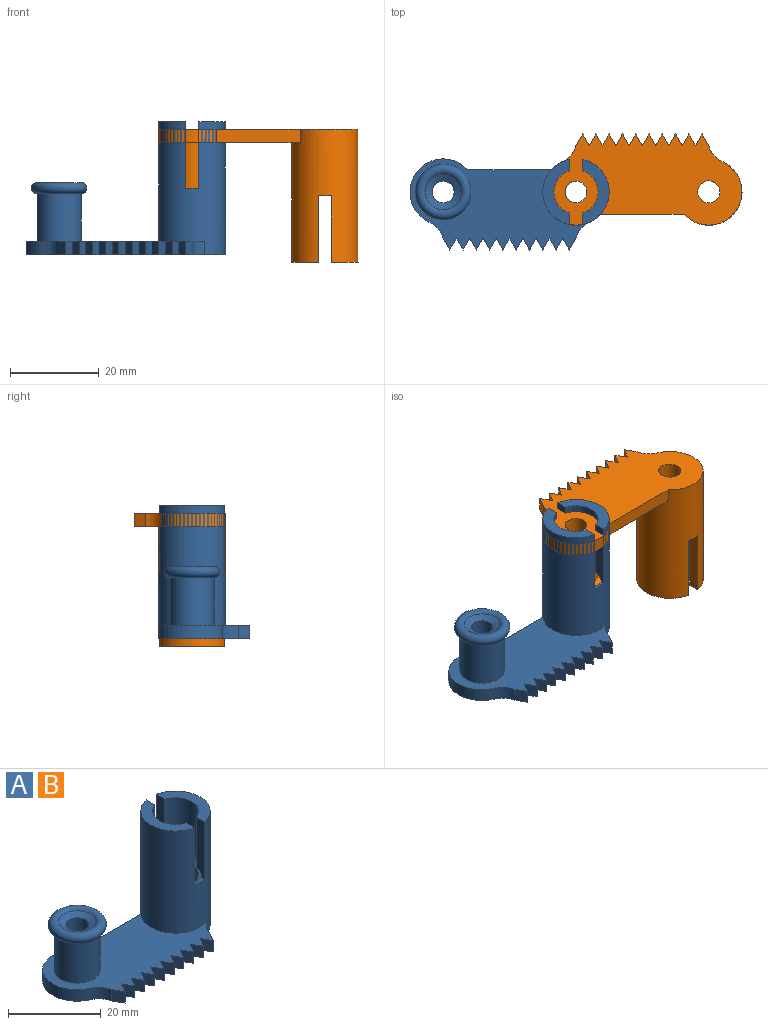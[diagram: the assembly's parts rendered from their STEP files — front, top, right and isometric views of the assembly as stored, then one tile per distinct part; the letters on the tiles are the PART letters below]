
ASSEMBLY  parts=2 mates=1
PART A: 45 faces, bbox 45x20.6x30 mm
  f0: sphere r=5mm, area 136mm2, adj f18,f22
  f1: cylinder r=5mm len=13.25mm, axis (0,0,-1), area 167.8mm2, adj f3,f6,f14,f17
  f2: cylinder r=5mm len=13.25mm, axis (0,0,-1), area 167.8mm2, adj f4,f5,f7,f17
  f3: plane 15x2.58mm, normal (-1,0,0), area 36.2mm2, adj f1,f11,f14,f15,f17
  f4: plane 15x2.58mm, normal (1,0,0), area 36.2mm2, adj f2,f7,f11,f15,f17
  f5: plane 15x2.58mm, normal (1,0,0), area 36.2mm2, adj f2,f7,f11,f16,f17
  f6: plane 15x2.58mm, normal (-1,0,0), area 36.2mm2, adj f1,f11,f14,f16,f17
  f7: plane 14.7x6mm, normal (0,0,1), area 41.5mm2, adj f2,f4,f5,f11
  f8: plane 40.44x20.58mm, normal (0,0,1), area 449.2mm2, adj f9,f10,f11,f13,f23,f24,f25,f26
  f9: plane 18.82x3mm, normal (0,1,0), area 56.5mm2, adj f8,f10,f11,f12
  f10: cylinder r=7.5mm len=14.4mm, axis (0,0,-1), area 80.5mm2, adj f8,f9,f12,f44
  f11: cylinder r=7.5mm len=30mm, axis (0,0,-1), area 1262.3mm2, adj f3,f4,f5,f6,f7,f8,f9,f12
  f12: plane 45x20.58mm, normal (0,0,-1), area 665.9mm2, adj f9,f10,f11,f21,f22,f23,f24,f25
  f13: cylinder r=5mm len=10.75mm, axis (0,0,-1), area 337.7mm2, adj f8,f19
  f14: plane 14.7x6mm, normal (0,0,1), area 41.5mm2, adj f1,f3,f6,f11
  f15: plane 3x0.92mm, normal (0,0,1), area 2.3mm2, adj f3,f4,f11,f17
  f16: plane 3x0.92mm, normal (0,0,1), area 2.3mm2, adj f5,f6,f11,f17
  f17: torus R=5mm, axis (0,0,1), area 194.5mm2, adj f1,f2,f3,f4,f5,f6,f15,f16
  f18: cylinder r=5mm len=10mm, axis (0,0,-1), area 164.9mm2, adj f0,f17
  f19: torus R=5.01mm, axis (0,0,1), area 175.8mm2, adj f13,f20
  f20: cone r=4.03mm half-angle=64deg, axis (0,0,1), area 35.7mm2, adj f19,f21
  f21: cylinder r=2.45mm len=15mm, axis (0,0,1), area 231.2mm2, adj f12,f20
  f22: cylinder r=2.5mm len=5mm, axis (0,0,-1), area 57.6mm2, adj f0,f12
  f23: plane 3x2.58mm, normal (0.86,-0.5,0), area 9mm2, adj f8,f12,f24,f42
  f24: plane 3x2.58mm, normal (-0.86,-0.5,0), area 9mm2, adj f8,f12,f23,f25
  f25: plane 3x2.58mm, normal (0.86,-0.5,0), area 9mm2, adj f8,f12,f24,f26
  f26: plane 3x2.58mm, normal (-0.86,-0.5,0), area 9mm2, adj f8,f12,f25,f27
  f27: plane 3x2.58mm, normal (0.86,-0.5,0), area 9mm2, adj f8,f12,f26,f28
  f28: plane 3x2.58mm, normal (-0.86,-0.5,0), area 9mm2, adj f8,f12,f27,f29
  f29: plane 3x2.58mm, normal (0.86,-0.5,0), area 9mm2, adj f8,f12,f28,f30
  f30: plane 3x2.58mm, normal (-0.86,-0.5,0), area 9mm2, adj f8,f12,f29,f31
  f31: plane 3x2.58mm, normal (0.86,-0.5,0), area 9mm2, adj f8,f12,f30,f32
  f32: plane 3x2.58mm, normal (-0.86,-0.5,0), area 9mm2, adj f8,f12,f31,f33
  f33: plane 3x2.58mm, normal (0.86,-0.5,0), area 9mm2, adj f8,f12,f32,f34
  f34: plane 3x2.58mm, normal (-0.86,-0.5,0), area 9mm2, adj f8,f12,f33,f35
  f35: plane 3x2.58mm, normal (0.86,-0.5,0), area 9mm2, adj f8,f12,f34,f36
  f36: plane 3x2.58mm, normal (-0.86,-0.5,0), area 9mm2, adj f8,f12,f35,f37
  f37: plane 3x2.58mm, normal (0.86,-0.5,0), area 9mm2, adj f8,f12,f36,f38
  f38: plane 3x2.58mm, normal (-0.86,-0.5,0), area 9mm2, adj f8,f12,f37,f39
  f39: plane 3x2.58mm, normal (0.86,-0.5,0), area 9mm2, adj f8,f12,f38,f40
  f40: plane 3x2.58mm, normal (-0.86,-0.5,0), area 9mm2, adj f8,f12,f39,f41
  f41: plane 3x2.58mm, normal (0.86,-0.5,0), area 9mm2, adj f8,f12,f40,f43
  f42: plane 3x2.58mm, normal (-0.86,-0.5,0), area 9mm2, adj f8,f12,f23,f44
  f43: cylinder r=5mm len=3.6mm, axis (0,0,-1), area 14.5mm2, adj f8,f11,f12,f41
  f44: cylinder r=5mm len=3.6mm, axis (0,0,-1), area 14.5mm2, adj f8,f10,f12,f42
PART B: same geometry as A
PLACE A rot(axis=(0.08,0.68,-0.73),0deg) t=(-17.72,-0.71,0.58)mm
PLACE B rot(axis=(-1,0,0),180deg) t=(12.28,-10.71,28.83)mm
MATE revolute B.f10 <-> A.f17  axis (0,0,-1) through (-17.72,-5.71,13.83)mm
